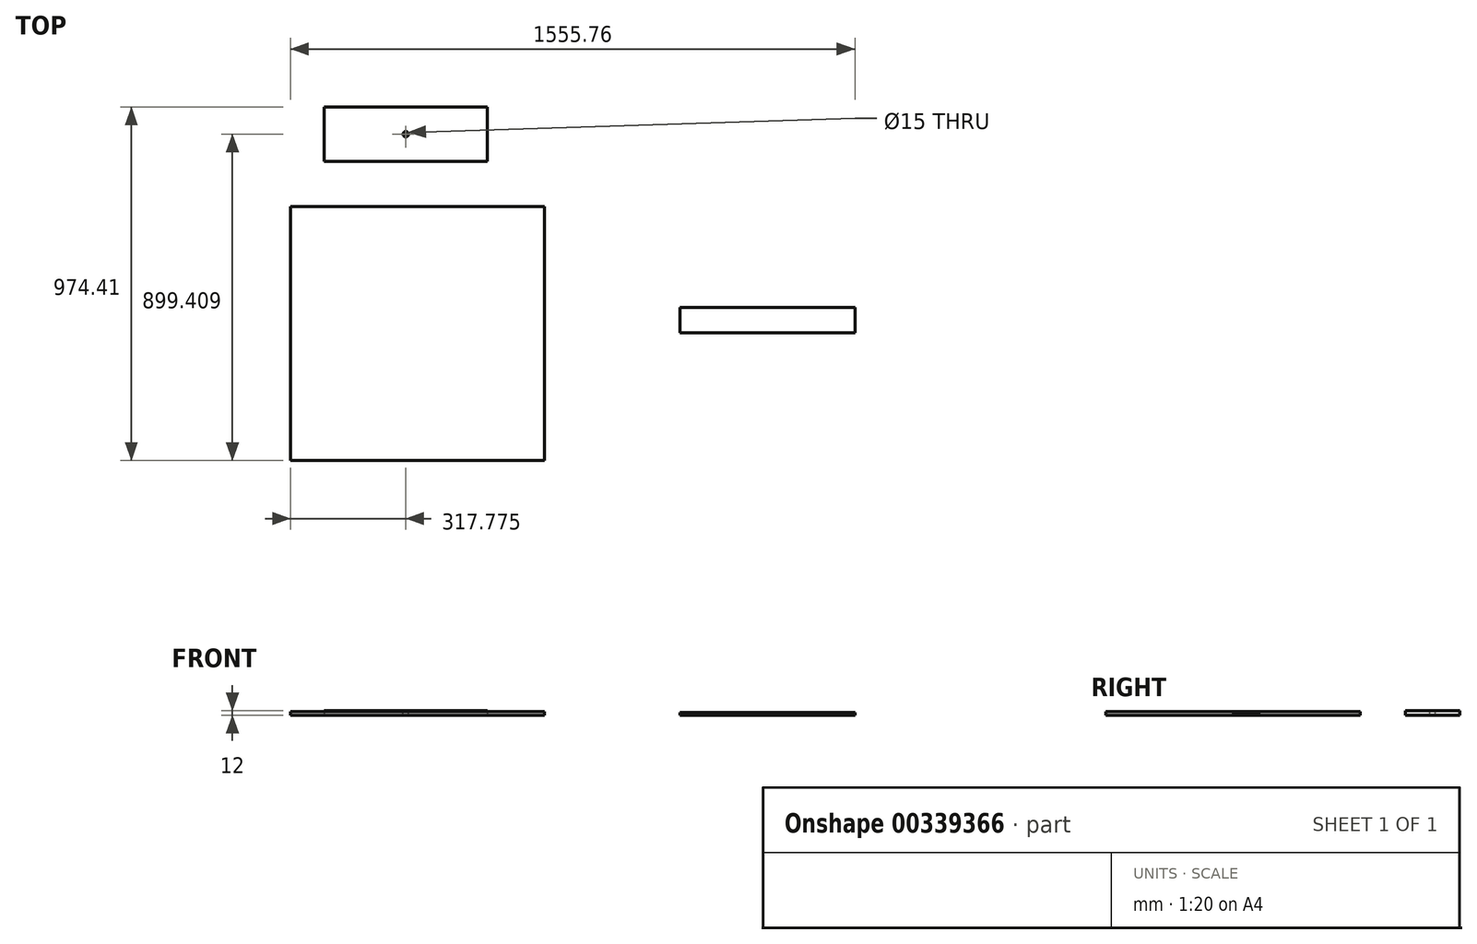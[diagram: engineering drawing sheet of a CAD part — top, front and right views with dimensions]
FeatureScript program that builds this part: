
annotation { "Feature Type Name" : "Feature", "Feature Type Description" : "" }
export const myFeature = defineFeature(function(context is Context, id is Id, definition is map)
    precondition{}
    {
        {
            var Q0;
            Q0=qCreatedBy(makeId("Top.planeOp"),FACE);
            var sketch = newSketch(context, id + "F0", { "sketchPlane" : qUnion([Q0])});
            skLineSegment(sketch, "E0.bottom", {"start": v(-350, 350) * mm, "end": v(350, 350) * mm});
            skLineSegment(sketch, "E0.top", {"start": v(-350, -350) * mm, "end": v(350, -350) * mm});
            skLineSegment(sketch, "E0.left", {"start": v(-350, 350) * mm, "end": v(-350, -350) * mm});
            skLineSegment(sketch, "E0.right", {"start": v(350, 350) * mm, "end": v(350, -350) * mm});
            skLineSegment(sketch, "E1", {"start": v(-350, 350) * mm, "end": v(350, -350) * mm});
            skSolve(sketch);
        }
        {
            var Q0;
            Q0=makeQuery(id+"F0.imprint","IMPRINT",FACE,{"disambiguationData":[TD([[makeQuery(id+"F0.imprint","IMPRINT",EDGE,{"derivedFrom":sQuery(id+"F0.wireOp",EDGE,"E0.top")}),1.0]])]});
            var Q1;
            Q1=makeQuery(id+"F0.imprint","IMPRINT",FACE,{"disambiguationData":[TD([[makeQuery(id+"F0.imprint","IMPRINT",EDGE,{"derivedFrom":sQuery(id+"F0.wireOp",EDGE,"E0.bottom")}),-1.0]])]});
            extrude(context, id + "F1", {"entities" : qUnion([Q0, Q1]), "depth" : 10 * mm});
        }
        {
            var Q0;
            Q0=qCreatedBy(makeId("Top.planeOp"),FACE);
            var sketch = newSketch(context, id + "F2", { "sketchPlane" : qUnion([Q0])});
            skLineSegment(sketch, "E2.bottom", {"start": v(722.76, 71.48) * mm, "end": v(1205.76, 71.48) * mm});
            skLineSegment(sketch, "E2.top", {"start": v(722.76, 1.48) * mm, "end": v(1205.76, 1.48) * mm});
            skLineSegment(sketch, "E2.left", {"start": v(722.76, 71.48) * mm, "end": v(722.76, 1.48) * mm});
            skLineSegment(sketch, "E2.right", {"start": v(1205.76, 71.48) * mm, "end": v(1205.76, 1.48) * mm});
            skSolve(sketch);
        }
        {
            var Q0;
            Q0=qSketchRegion(id+"F2",true);
            extrude(context, id + "F3", {"entities" : qUnion([Q0]), "depth" : 8 * mm});
        }
        {
            var Q0;
            Q0=qCreatedBy(makeId("Top.planeOp"),FACE);
            var sketch = newSketch(context, id + "F4", { "sketchPlane" : qUnion([Q0])});
            skLineSegment(sketch, "E3.bottom", {"start": v(-257.22, 624.4) * mm, "end": v(192.78, 624.4) * mm});
            skLineSegment(sketch, "E3.top", {"start": v(-257.22, 474.4) * mm, "end": v(192.78, 474.4) * mm});
            skLineSegment(sketch, "E3.left", {"start": v(-257.22, 624.4) * mm, "end": v(-257.22, 474.4) * mm});
            skLineSegment(sketch, "E3.right", {"start": v(192.78, 624.4) * mm, "end": v(192.78, 474.4) * mm});
            skSolve(sketch);
        }
        {
            var Q0;
            Q0=makeQuery(id+"F4.imprint","IMPRINT",FACE,{"disambiguationData":[TD([[makeQuery(id+"F4.imprint","IMPRINT",EDGE,{"derivedFrom":sQuery(id+"F4.wireOp",EDGE,"E3.bottom")}),-1.0]])]});
            extrude(context, id + "F5", {"entities" : qUnion([Q0]), "depth" : 12 * mm});
        }
        {
            var Q0;
            Q0=makeQuery(id+"F5.opExtrude","CAP_FACE",FACE,{"disambiguationData":[OSD([sQuery(id+"F4.wireOp",EDGE,"E3.bottom"),sQuery(id+"F4.wireOp",EDGE,"E3.top"),sQuery(id+"F4.wireOp",EDGE,"E3.left"),sQuery(id+"F4.wireOp",EDGE,"E3.right")])],"isStart":false});
            var sketch = newSketch(context, id + "F6", { "sketchPlane" : qUnion([Q0])});
            skCircle(sketch, "E4", {"center": v(-32.22, 549.4) * mm, "radius": 7.5 * mm});
            skLineSegment(sketch, "E5", {"start": v(-257.22, 624.4) * mm, "end": v(192.78, 474.4) * mm, "construction": true});
            skSolve(sketch);
        }
        {
            var Q0;
            Q0=makeQuery(id+"F6.imprint","IMPRINT",FACE,{"disambiguationData":[TD([[makeQuery(id+"F6.imprint","IMPRINT",EDGE,{"derivedFrom":sQuery(id+"F6.wireOp",EDGE,"E4")}),1.0]])]});
            extrude(context, id + "F7", {"entities" : qUnion([Q0]), "operationType" : NewBodyOperationType.REMOVE, "endBound" : BoundingType.THROUGH_ALL, "oppositeDirection" : true, "depth" : 25 * mm});
        }
    });
